# Revit family: BC_Hitachi_RCD-FSR-0.8-6.0_LOD400
name_source: partatom
category: Mechanical Equipment
revit_build: Autodesk Revit 2018 (Build: 20170223_1515(x64)
units: mm (PartAtom-declared; Revit-internal decimal feet)

## family parameters
Cut with Voids When Loaded = No
Host = Face
OmniClass Number = 23.75.70.00
OmniClass Title = HVAC Distribution Devices
Part Type = Normal
Room Calculation Point = No
Round Connector Dimension = Use Diameter
Shared = No

## types (9) — shared parameters
BC_OBJECT_ID = 209119
BC_OBJECT_VERSION = #10
Color = Spring white (4.1Y8.5/0.7)
Default Elevation = 1219.20 mm
Description = RCD - 2-way cassette
Description OmniClass = Air Handling Units
Duct adapter diameter = 150.00 mm
Face Depth = 30.00 mm
Face Width = 710.00 mm
Frequency = 50 Hz
Manufacturer = Hitachi Air Conditioning Europe SAS
MasterFormat = Indoor Central-Station Air-Handling Units
Masterformat Code = 23 73 00
Maximum AC Voltage = 253 V
Minimum AC Voltage = 207 V
Model = RCD - 2-way cassette
Name BIM&CO = Indoor Unit
Nominal Voltage = 230 V
Number of Poles = 1
OmniClass code = 23-33 25 00
OmniClass description = Air Handling Units
Outlet Diameter = 32.00 mm
Overall depth = 630.00 mm
Overall height = 298.00 mm
Refrigerant Type = R410A / R32
Uniformat = Distribution Systems
Uniformat code = D3040
Usage Current = 5 A
Wiring diameter = 26.00 mm

## per-type parameters (varying)
| type | Acoustic Pressure Level Maxi | Acoustic Pressure Level Medium (dB) | Acoustic Pressure Level Mini | Air Flow (HiH/Hi/Me/low) m3/min | BC_VARIANT_ID | Cooling Capacity | Face Length | Fan motor type (output) | Gas Diameter | Heating Capacity | Liquid Diameter | Mass | Maximum Air Flow | Minimum Air Flow | Overall width | Product Code | Sound power max | Type Comments |
| RCD-6.0FSR | 48 | 42 | 39 | 37/32.5/28.5/24 | 508773 | 14 kW | 1660.00 mm | 114 W | 15.88 mm | 17 kW | 9.52 mm | 39.00 kg | 2220.0 m³/h | 1440.0 m³/h | 1420.00 mm | 60279176 | 59 | RCD-6.0FSR |
| RCD-5.0FSR | 47 | 41 | 34 | 35/31/27/21 | 508772 | 13 kW | 1660.00 mm | 114 W | 15.88 mm | 14 kW | 9.52 mm | 39.00 kg | 2100.0 m³/h | 1260.0 m³/h | 1420.00 mm | 60279175 | 55 | RCD-5.0FSR |
| RCD-4.0FSR | 43 | 37 | 34 | 30/26.5/23/20 | 508774 | 10 kW | 1660.00 mm | 114 W | 15.88 mm | 11 kW | 9.52 mm | 39.00 kg | 1800.0 m³/h | 1200.0 m³/h | 1420.00 mm | 60279174 | 55 | RCD-4.0FSR |
| RCD-3.0FSR | 45 | 38 | 33 | 21/18.5/16/12.5 | 508771 | 7 kW | 1100.00 mm | 57 W | 15.88 mm | 8 kW | 9.52 mm | 25.00 kg | 1260.0 m³/h | 750.0 m³/h | 860.00 mm | 60279173 | 55 | RCD-3.0FSR |
| RCD-2.5FSR | 42 | 36 | 33 | 18.5/16.5/14.5/12.5 | 508769 | 6 kW | 1100.00 mm | 57 W | 15.88 mm | 6 kW | 9.52 mm | 25.00 kg | 1110.0 m³/h | 750.0 m³/h | 860.00 mm | 60279172 | 52 | RCD-2.5FSR |
| RCD-2.0FSR | 39 | 33 | 30 | 16.5/14.5/12.5/10.5 | 508767 | 5 kW | 1100.00 mm | 57 W | 12.70 mm | 6 kW | 6.35 mm | 25.00 kg | 990.0 m³/h | 630.0 m³/h | 860.00 mm | 60279171 | 51 | RCD-2.0FSR |
| RCD-1.5FSR | 37 | 31 | 30 | 15/13/11.5/10 | 508770 | 4 kW | 1100.00 mm | 57 W | 12.70 mm | 4 kW | 6.35 mm | 25.00 kg | 900.0 m³/h | 600.0 m³/h | 860.00 mm | 60279170 | 49 | RCD-1.5FSR |
| RCD-1.0FSR | 31 | 28 | 27 | 11/9.5/8.5/7 | 508775 | 3 kW | 1100.00 mm | 57 W | 12.70 mm | 3 kW | 6.35 mm | 23.00 kg | 660.0 m³/h | 420.0 m³/h | 860.00 mm | 60279169 | 46 | RCD-0.8FSR |
| RCD-0.8FSR | 30 | 28 | 27 | 10/9/7.5/6.5 | 508768 | 2 kW | 1100.00 mm | 57 W | 12.70 mm | 2 kW | 6.35 mm | 23.00 kg | 600.0 m³/h | 390.0 m³/h | 860.00 mm | 60279168 | 44 | RCD-0.8FSR |

note: column(s) folded — value = type name in every type: Reference
